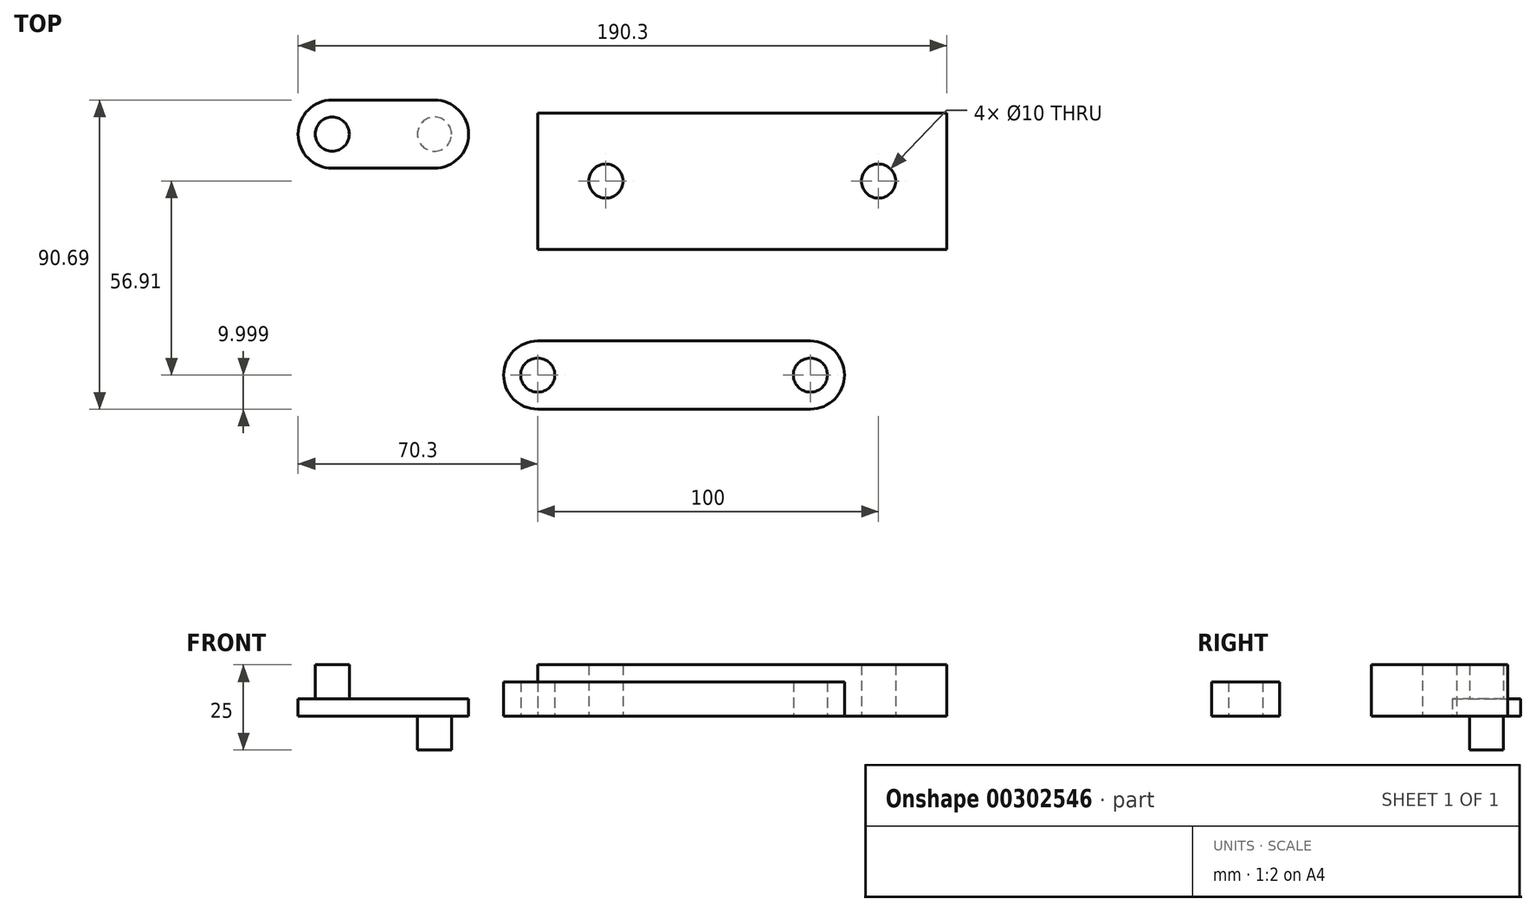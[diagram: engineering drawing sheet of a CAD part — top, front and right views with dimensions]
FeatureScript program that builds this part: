
annotation { "Feature Type Name" : "Feature", "Feature Type Description" : "" }
export const myFeature = defineFeature(function(context is Context, id is Id, definition is map)
    precondition{}
    {
        {
            var Q0;
            Q0=qCreatedBy(makeId("Top.planeOp"),FACE);
            var sketch = newSketch(context, id + "F0", { "sketchPlane" : qUnion([Q0])});
            skLineSegment(sketch, "E0.bottom", {"start": v(0, 0) * mm, "end": v(120, 0) * mm});
            skLineSegment(sketch, "E0.top", {"start": v(0, 40) * mm, "end": v(120, 40) * mm});
            skLineSegment(sketch, "E0.left", {"start": v(0, 0) * mm, "end": v(0, 40) * mm});
            skLineSegment(sketch, "E0.right", {"start": v(120, 0) * mm, "end": v(120, 40) * mm});
            skCircle(sketch, "E1", {"center": v(20, 20) * mm, "radius": 5 * mm});
            skPoint(sketch, "E2.centerSnap0", {"position": v(120, 20) * mm});
            skCircle(sketch, "E3", {"center": v(100, 20) * mm, "radius": 5 * mm});
            skLineSegment(sketch, "E4", {"start": v(-60.3, 43.78) * mm, "end": v(-30.3, 43.78) * mm});
            skLineSegment(sketch, "E5", {"start": v(-30.3, 23.78) * mm, "end": v(-60.3, 23.78) * mm});
            skCircle(sketch, "E6", {"center": v(-30.3, 33.78) * mm, "radius": 5 * mm});
            skCircle(sketch, "E7", {"center": v(-60.3, 33.78) * mm, "radius": 5 * mm});
            skArc(sketch, "E8", {"start": v(-30.3, 23.78) * mm, "mid": v(-20.3, 33.78) * mm, "end": v(-30.3, 43.78) * mm});
            skArc(sketch, "E9", {"start": v(-60.3, 43.78) * mm, "mid": v(-70.3, 33.78) * mm, "end": v(-60.3, 23.78) * mm});
            skLineSegment(sketch, "E10", {"start": v(0, -26.91) * mm, "end": v(80, -26.91) * mm});
            skCircle(sketch, "E11", {"center": v(80, -36.91) * mm, "radius": 5 * mm});
            skCircle(sketch, "E12", {"center": v(0, -36.91) * mm, "radius": 5 * mm});
            skArc(sketch, "E13", {"start": v(80, -46.91) * mm, "mid": v(90, -36.91) * mm, "end": v(80, -26.91) * mm});
            skLineSegment(sketch, "E14", {"start": v(80, -46.91) * mm, "end": v(0, -46.91) * mm});
            skArc(sketch, "E15", {"start": v(0, -26.91) * mm, "mid": v(-10, -36.91) * mm, "end": v(0, -46.91) * mm});
            skSolve(sketch);
        }
        {
            var Q0;
            Q0=makeQuery(id+"F0.imprint","IMPRINT",FACE,{"disambiguationData":[TD([[makeQuery(id+"F0.imprint","IMPRINT",EDGE,{"derivedFrom":sQuery(id+"F0.wireOp",EDGE,"E0.bottom")}),1.0]])]});
            extrude(context, id + "F1", {"entities" : qUnion([Q0]), "depth" : 15 * mm});
        }
        {
            var Q0;
            Q0=makeQuery(id+"F0.imprint","IMPRINT",FACE,{"disambiguationData":[TD([[makeQuery(id+"F0.imprint","IMPRINT",EDGE,{"derivedFrom":sQuery(id+"F0.wireOp",EDGE,"E4")}),-1.0]])]});
            extrude(context, id + "F2", {"entities" : qUnion([Q0]), "depth" : 5 * mm});
        }
        {
            var Q0;
            Q0=makeQuery(id+"F0.imprint","IMPRINT",FACE,{"disambiguationData":[TD([[makeQuery(id+"F0.imprint","IMPRINT",EDGE,{"derivedFrom":sQuery(id+"F0.wireOp",EDGE,"E7")}),1.0]])]});
            var Q1;
            Q1=sQuery(id+"F0.wireOp",EDGE,"E7");
            extrude(context, id + "F3", {"entities" : qUnion([Q0]), "operationType" : NewBodyOperationType.ADD, "surfaceEntities" : qUnion([Q1]), "depth" : 15 * mm});
        }
        {
            var Q0;
            Q0=makeQuery(id+"F0.imprint","IMPRINT",FACE,{"disambiguationData":[TD([[makeQuery(id+"F0.imprint","IMPRINT",EDGE,{"derivedFrom":sQuery(id+"F0.wireOp",EDGE,"E6")}),1.0]])]});
            extrude(context, id + "F4", {"entities" : qUnion([Q0]), "operationType" : NewBodyOperationType.ADD, "oppositeDirection" : true, "depth" : 10 * mm, "hasSecondDirection" : true, "secondDirectionOppositeDirection" : false, "secondDirectionDepth" : 5 * mm});
        }
        {
            var Q0;
            Q0=makeQuery(id+"F0.imprint","IMPRINT",FACE,{"disambiguationData":[TD([[makeQuery(id+"F0.imprint","IMPRINT",EDGE,{"derivedFrom":sQuery(id+"F0.wireOp",EDGE,"E10")}),-1.0]])]});
            extrude(context, id + "F5", {"entities" : qUnion([Q0]), "depth" : 10 * mm});
        }
    });
